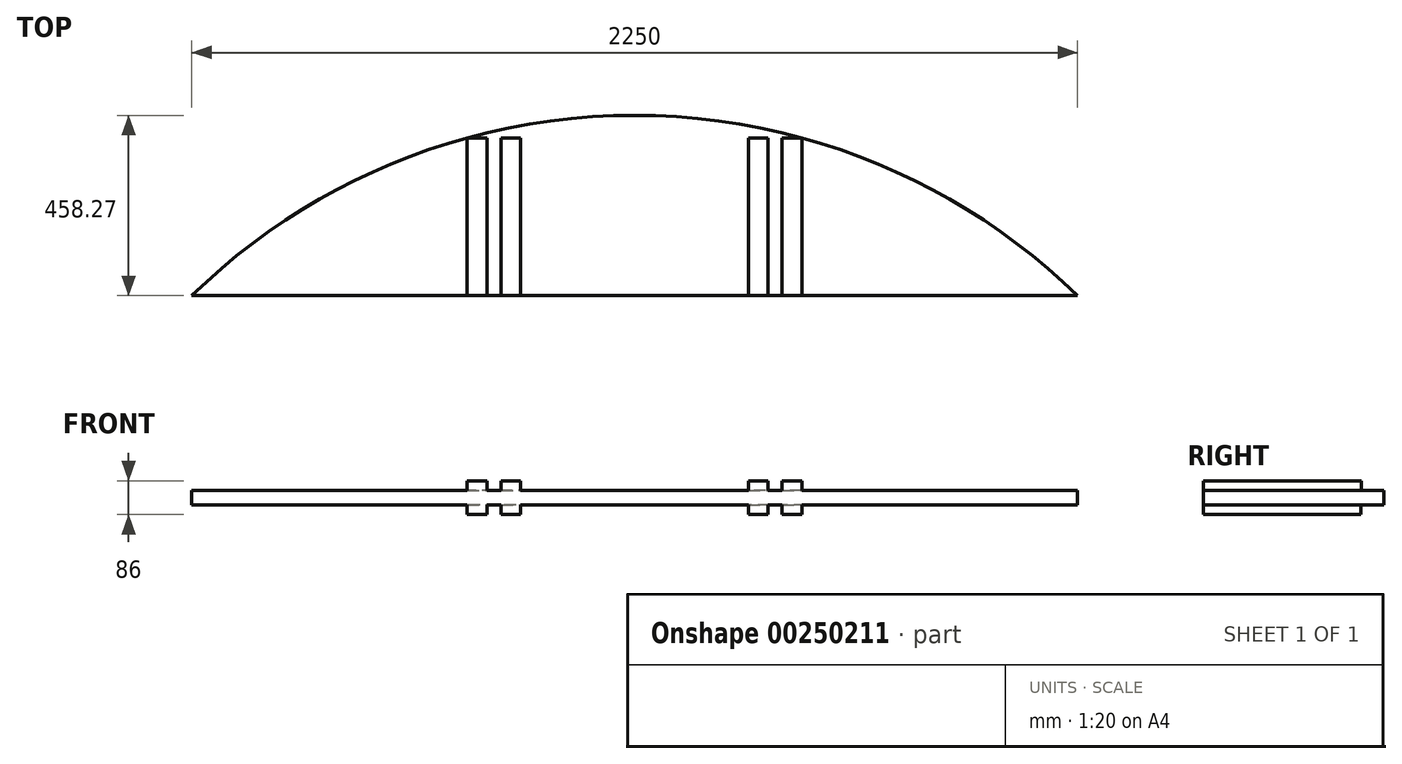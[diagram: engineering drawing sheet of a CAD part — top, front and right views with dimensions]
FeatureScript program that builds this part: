
annotation { "Feature Type Name" : "Feature", "Feature Type Description" : "" }
export const myFeature = defineFeature(function(context is Context, id is Id, definition is map)
    precondition{}
    {
        {
            var Q0;
            Q0=qCreatedBy(makeId("Top.planeOp"),FACE);
            var sketch = newSketch(context, id + "F0", { "sketchPlane" : qUnion([Q0])});
            skArc(sketch, "E0", {"start": v(1125, 1151.73) * mm, "mid": v(0, 1610) * mm, "end": v(-1125, 1151.73) * mm});
            skLineSegment(sketch, "E1", {"start": v(-1125, 1151.73) * mm, "end": v(1125, 1151.73) * mm});
            skSolve(sketch);
        }
        {
            var Q0;
            Q0=qSketchRegion(id+"F0",true);
            extrude(context, id + "F1", {"entities" : qUnion([Q0]), "depth" : 36 * mm});
        }
        {
            var Q0;
            Q0=makeQuery(id+"F1.opExtrude","CAP_FACE",FACE,{"disambiguationData":[OSD([sQuery(id+"F0.wireOp",EDGE,"E0"),sQuery(id+"F0.wireOp",EDGE,"E1")])],"isStart":false});
            var sketch = newSketch(context, id + "F2", { "sketchPlane" : qUnion([Q0])});
            skLineSegment(sketch, "E2.bottom", {"start": v(-425, 1552.9) * mm, "end": v(-375, 1552.9) * mm});
            skLineSegment(sketch, "E2.top", {"start": v(-425, 1151.73) * mm, "end": v(-375, 1151.73) * mm});
            skLineSegment(sketch, "E2.left", {"start": v(-425, 1552.9) * mm, "end": v(-425, 1151.73) * mm});
            skLineSegment(sketch, "E2.right", {"start": v(-375, 1552.9) * mm, "end": v(-375, 1151.73) * mm});
            skLineSegment(sketch, "E3.bottom", {"start": v(375, 1151.73) * mm, "end": v(425, 1151.73) * mm});
            skLineSegment(sketch, "E3.top", {"start": v(375, 1552.9) * mm, "end": v(425, 1552.9) * mm});
            skLineSegment(sketch, "E3.left", {"start": v(375, 1151.73) * mm, "end": v(375, 1552.9) * mm});
            skLineSegment(sketch, "E3.right", {"start": v(425, 1151.73) * mm, "end": v(425, 1552.9) * mm});
            skLineSegment(sketch, "E4.bottom", {"start": v(-339, 1551.73) * mm, "end": v(-289, 1551.73) * mm});
            skLineSegment(sketch, "E4.top", {"start": v(-339, 1151.73) * mm, "end": v(-289, 1151.73) * mm});
            skLineSegment(sketch, "E4.left", {"start": v(-339, 1551.73) * mm, "end": v(-339, 1151.73) * mm});
            skLineSegment(sketch, "E4.right", {"start": v(-289, 1551.73) * mm, "end": v(-289, 1151.73) * mm});
            skLineSegment(sketch, "E5.bottom", {"start": v(289, 1551.73) * mm, "end": v(339, 1551.73) * mm});
            skLineSegment(sketch, "E5.top", {"start": v(289, 1151.73) * mm, "end": v(339, 1151.73) * mm});
            skLineSegment(sketch, "E5.left", {"start": v(289, 1551.73) * mm, "end": v(289, 1151.73) * mm});
            skLineSegment(sketch, "E5.right", {"start": v(339, 1551.73) * mm, "end": v(339, 1151.73) * mm});
            skSolve(sketch);
        }
        {
            var Q0;
            Q0=qSketchRegion(id+"F2",true);
            extrude(context, id + "F3", {"entities" : qUnion([Q0]), "operationType" : NewBodyOperationType.ADD, "depth" : 25 * mm});
        }
        {
            var Q0;
            Q0=qSketchRegion(id+"F2",true);
            extrude(context, id + "F4", {"entities" : qUnion([Q0]), "operationType" : NewBodyOperationType.ADD, "depth" : 25 * mm});
        }
        {
            var Q0;
            Q0=makeQuery(id+"F1.opExtrude","CAP_FACE",FACE,{"disambiguationData":[OSD([sQuery(id+"F0.wireOp",EDGE,"E0"),sQuery(id+"F0.wireOp",EDGE,"E1")])],"isStart":true});
            var sketch = newSketch(context, id + "F5", { "sketchPlane" : qUnion([Q0])});
            skLineSegment(sketch, "E6.bottom", {"start": v(-425, -1151.73) * mm, "end": v(-375, -1151.73) * mm});
            skLineSegment(sketch, "E6.top", {"start": v(-425, -1551.73) * mm, "end": v(-375, -1551.73) * mm});
            skLineSegment(sketch, "E6.left", {"start": v(-425, -1151.73) * mm, "end": v(-425, -1551.73) * mm});
            skLineSegment(sketch, "E6.right", {"start": v(-375, -1151.73) * mm, "end": v(-375, -1551.73) * mm});
            skLineSegment(sketch, "E7.bottom", {"start": v(-339, -1151.73) * mm, "end": v(-289, -1151.73) * mm});
            skLineSegment(sketch, "E7.top", {"start": v(-339, -1551.08) * mm, "end": v(-289, -1551.08) * mm});
            skLineSegment(sketch, "E7.left", {"start": v(-339, -1151.73) * mm, "end": v(-339, -1551.08) * mm});
            skLineSegment(sketch, "E7.right", {"start": v(-289, -1151.73) * mm, "end": v(-289, -1551.08) * mm});
            skLineSegment(sketch, "E8.bottom", {"start": v(375, -1151.73) * mm, "end": v(425, -1151.73) * mm});
            skLineSegment(sketch, "E8.top", {"start": v(375, -1551.73) * mm, "end": v(425, -1551.73) * mm});
            skLineSegment(sketch, "E8.left", {"start": v(375, -1151.73) * mm, "end": v(375, -1551.73) * mm});
            skLineSegment(sketch, "E8.right", {"start": v(425, -1151.73) * mm, "end": v(425, -1551.73) * mm});
            skLineSegment(sketch, "E9.bottom", {"start": v(289, -1151.73) * mm, "end": v(339, -1151.73) * mm});
            skLineSegment(sketch, "E9.top", {"start": v(289, -1551.73) * mm, "end": v(339, -1551.73) * mm});
            skLineSegment(sketch, "E9.left", {"start": v(289, -1151.73) * mm, "end": v(289, -1551.73) * mm});
            skLineSegment(sketch, "E9.right", {"start": v(339, -1151.73) * mm, "end": v(339, -1551.73) * mm});
            skSolve(sketch);
        }
        {
            var Q0;
            Q0=makeQuery(id+"F5.imprint","IMPRINT",FACE,{"disambiguationData":[TD([[makeQuery(id+"F5.imprint","IMPRINT",EDGE,{"derivedFrom":sQuery(id+"F5.wireOp",EDGE,"E9.bottom")}),-1.0]])]});
            var Q1;
            Q1=makeQuery(id+"F5.imprint","IMPRINT",FACE,{"disambiguationData":[TD([[makeQuery(id+"F5.imprint","IMPRINT",EDGE,{"derivedFrom":sQuery(id+"F5.wireOp",EDGE,"E8.bottom")}),-1.0]])]});
            var Q2;
            Q2=makeQuery(id+"F5.imprint","IMPRINT",FACE,{"disambiguationData":[TD([[makeQuery(id+"F5.imprint","IMPRINT",EDGE,{"derivedFrom":sQuery(id+"F5.wireOp",EDGE,"E7.bottom")}),-1.0]])]});
            var Q3;
            Q3=makeQuery(id+"F5.imprint","IMPRINT",FACE,{"disambiguationData":[TD([[makeQuery(id+"F5.imprint","IMPRINT",EDGE,{"derivedFrom":sQuery(id+"F5.wireOp",EDGE,"E6.bottom")}),-1.0]])]});
            extrude(context, id + "F6", {"entities" : qUnion([Q0, Q1, Q2, Q3]), "operationType" : NewBodyOperationType.ADD, "depth" : 25 * mm});
        }
    });
